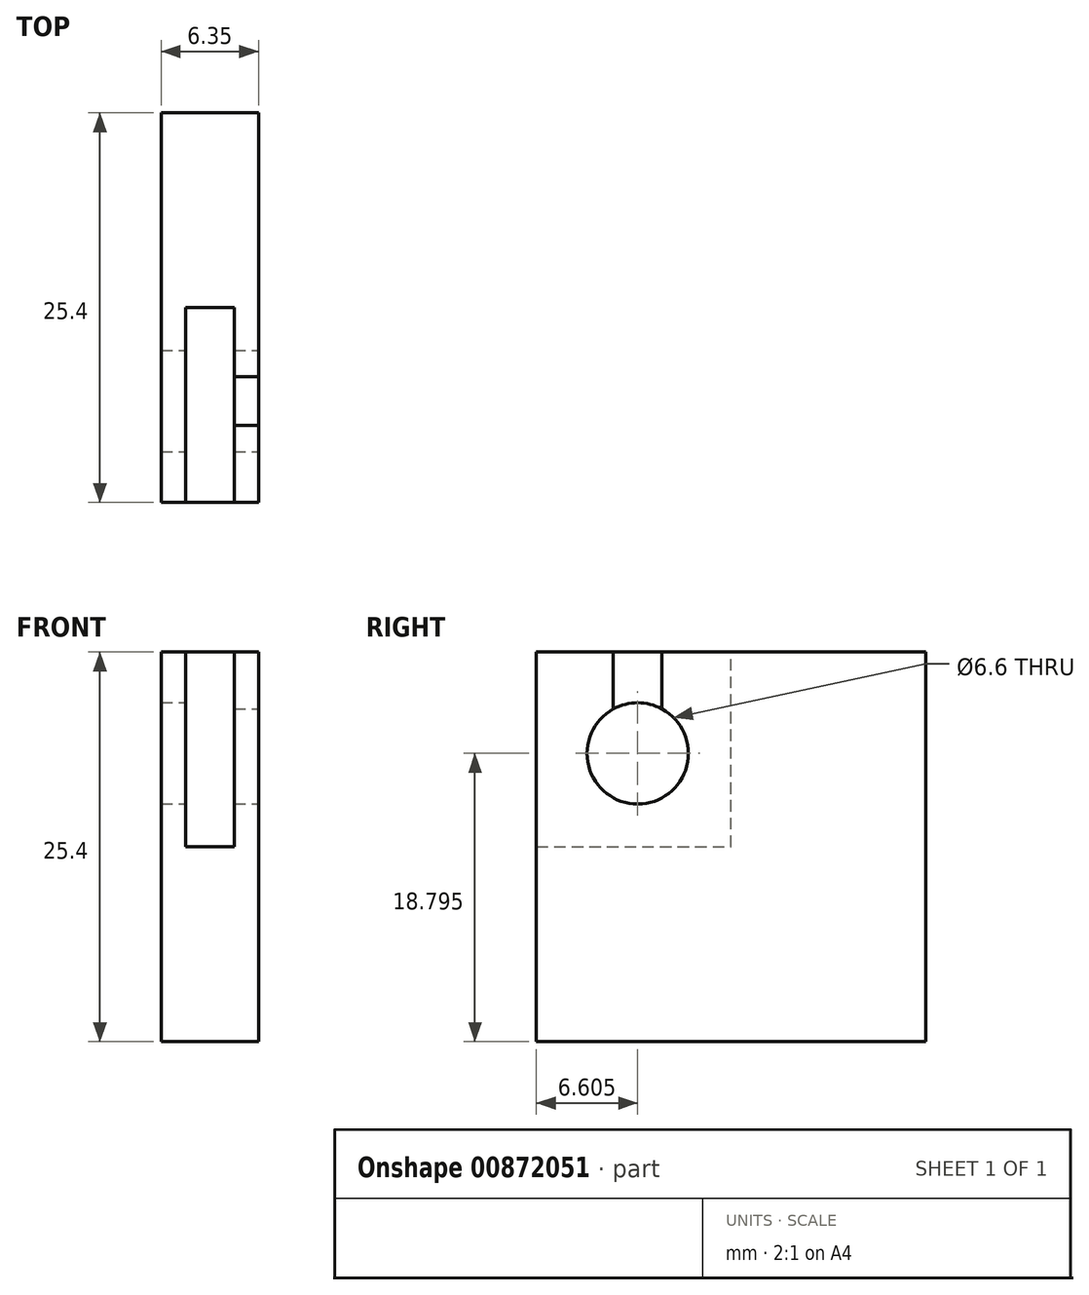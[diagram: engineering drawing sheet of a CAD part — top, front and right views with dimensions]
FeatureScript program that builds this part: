
annotation { "Feature Type Name" : "Feature", "Feature Type Description" : "" }
export const myFeature = defineFeature(function(context is Context, id is Id, definition is map)
    precondition{}
    {
        {
            var Q0;
            Q0=qCreatedBy(makeId("Right.planeOp"),FACE);
            var sketch = newSketch(context, id + "F0", { "sketchPlane" : qUnion([Q0])});
            skLineSegment(sketch, "E0.bottom", {"start": v(-7.25, 15.73) * mm, "end": v(18.15, 15.73) * mm});
            skLineSegment(sketch, "E0.top", {"start": v(-7.25, -9.67) * mm, "end": v(18.15, -9.67) * mm});
            skLineSegment(sketch, "E0.left", {"start": v(-7.25, 15.73) * mm, "end": v(-7.25, -9.67) * mm});
            skLineSegment(sketch, "E0.right", {"start": v(18.15, 15.73) * mm, "end": v(18.15, -9.67) * mm});
            skSolve(sketch);
        }
        {
            var Q0;
            Q0 = qSketchRegion(id + "F0", true);
            extrude(context, id + "F1", {"entities" : qUnion([Q0]), "depth" : 6.35 * mm, "offsetDistance" : 25.4 * mm});
        }
        {
            var Q0;
            Q0=makeQuery(id+"F1.opExtrude","CAP_FACE",FACE,{"disambiguationData":[OSD([sQuery(id+"F0.wireOp",EDGE,"E0.bottom"),sQuery(id+"F0.wireOp",EDGE,"E0.top"),sQuery(id+"F0.wireOp",EDGE,"E0.left"),sQuery(id+"F0.wireOp",EDGE,"E0.right")])],"isStart":false});
            var sketch = newSketch(context, id + "F2", { "sketchPlane" : qUnion([Q0])});
            skCircle(sketch, "E1", {"center": v(-0.65, 9.13) * mm, "radius": 3.3 * mm});
            skSolve(sketch);
        }
        {
            var Q0;
            Q0 = qSketchRegion(id + "F2", true);
            extrude(context, id + "F3", {"entities" : qUnion([Q0]), "operationType" : NewBodyOperationType.REMOVE, "oppositeDirection" : true, "depth" : 25.4 * mm, "offsetDistance" : 25.4 * mm});
        }
        {
            var Q0;
            Q0=makeQuery(id+"F1.opExtrude","SWEPT_FACE",FACE,{"disambiguationData":[OSD([sQuery(id+"F0.wireOp",EDGE,"E0.bottom")])]});
            var sketch = newSketch(context, id + "F4", { "sketchPlane" : qUnion([Q0])});
            skLineSegment(sketch, "E2.bottom", {"start": v(1.59, -7.25) * mm, "end": v(4.76, -7.25) * mm});
            skLineSegment(sketch, "E2.top", {"start": v(1.59, 5.45) * mm, "end": v(4.76, 5.45) * mm});
            skLineSegment(sketch, "E2.left", {"start": v(1.59, -7.25) * mm, "end": v(1.59, 5.45) * mm});
            skLineSegment(sketch, "E2.right", {"start": v(4.76, -7.25) * mm, "end": v(4.76, 5.45) * mm});
            skSolve(sketch);
        }
        {
            var Q0;
            Q0 = qSketchRegion(id + "F4", true);
            extrude(context, id + "F5", {"entities" : qUnion([Q0]), "operationType" : NewBodyOperationType.REMOVE, "oppositeDirection" : true, "depth" : 12.7 * mm, "offsetDistance" : 25.4 * mm});
        }
        {
            var Q0;
            Q0=makeQuery(id+"F1.opExtrude","SWEPT_FACE",FACE,{"disambiguationData":[OSD([sQuery(id+"F0.wireOp",EDGE,"E0.bottom")])]});
            var sketch = newSketch(context, id + "F6", { "sketchPlane" : qUnion([Q0])});
            skLineSegment(sketch, "E3.bottom", {"start": v(1.59, -2.23) * mm, "end": v(6.35, -2.23) * mm});
            skLineSegment(sketch, "E3.top", {"start": v(1.59, 0.94) * mm, "end": v(6.35, 0.94) * mm});
            skLineSegment(sketch, "E3.left", {"start": v(0, -2.23) * mm, "end": v(0, 0.94) * mm, "construction": true});
            skLineSegment(sketch, "E3.right", {"start": v(6.35, -2.23) * mm, "end": v(6.35, 0.94) * mm});
            skLineSegment(sketch, "E4", {"start": v(6.88, -0.65) * mm, "end": v(-0.5, -0.65) * mm, "construction": true});
            skPoint(sketch, "E4.startSnap0", {"position": v(6.35, -0.65) * mm});
            skLineSegment(sketch, "E5", {"start": v(1.59, 0.94) * mm, "end": v(1.59, -2.23) * mm});
            skSolve(sketch);
        }
        {
            var Q0;
            Q0 = qSketchRegion(id + "F6", true);
            extrude(context, id + "F7", {"entities" : qUnion([Q0]), "operationType" : NewBodyOperationType.REMOVE, "oppositeDirection" : true, "depth" : 6.6 * mm, "offsetDistance" : 25.4 * mm});
        }
    });
